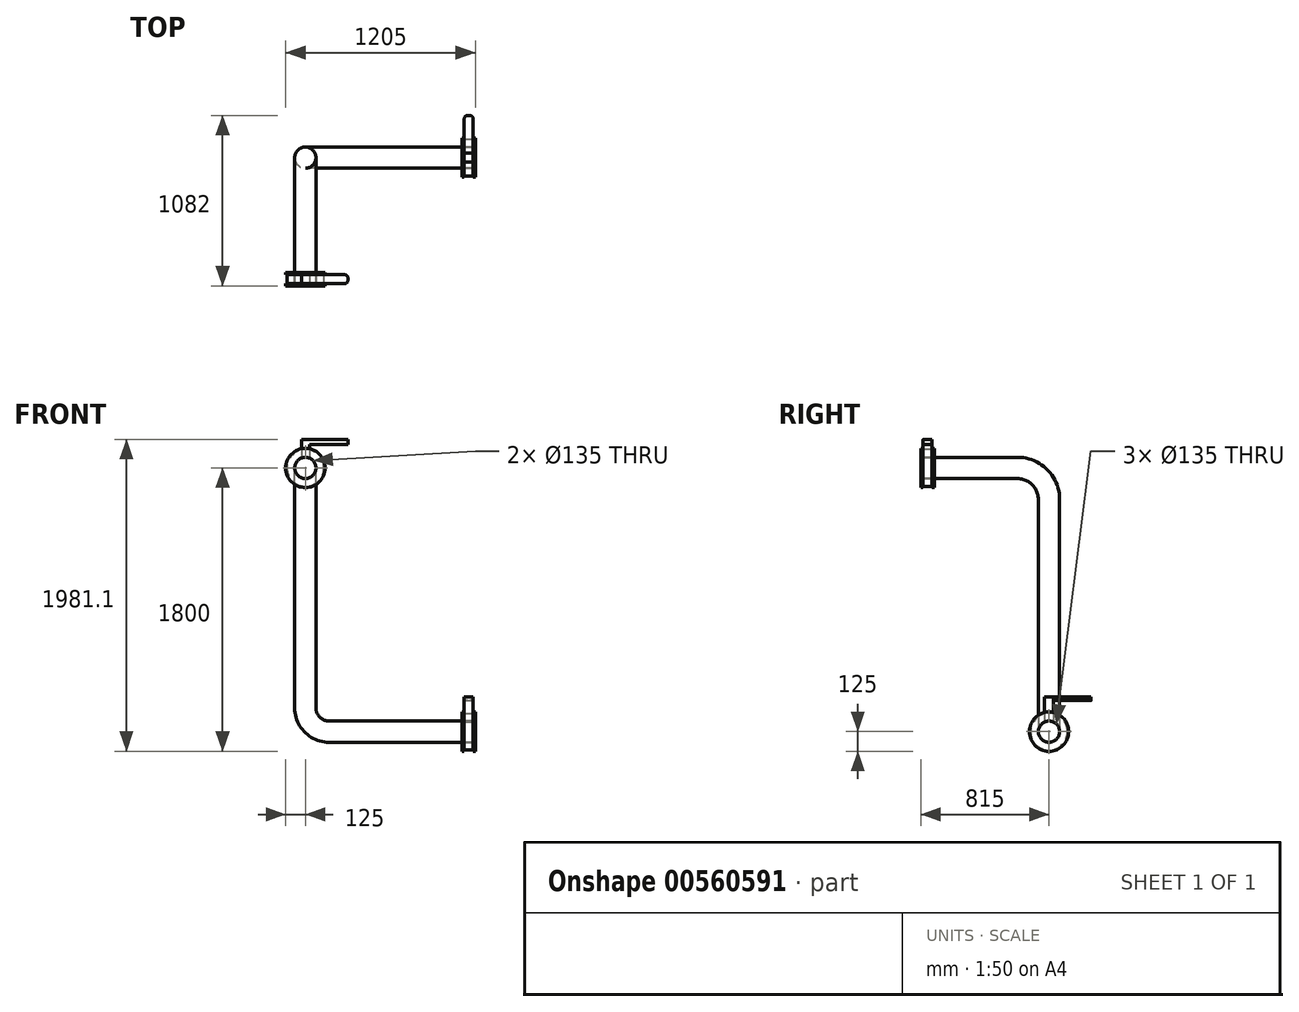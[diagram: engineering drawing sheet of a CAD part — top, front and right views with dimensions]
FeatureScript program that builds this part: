
annotation { "Feature Type Name" : "Feature", "Feature Type Description" : "" }
export const myFeature = defineFeature(function(context is Context, id is Id, definition is map)
    precondition{}
    {
        {
            var Q0;
            Q0=qCreatedBy(makeId("Front.planeOp"),FACE);
            var sketch = newSketch(context, id + "F0", { "sketchPlane" : qUnion([Q0])});
            skCircle(sketch, "E0", {"center": v(0, 0) * mm, "radius": 125 * mm});
            skCircle(sketch, "E1", {"center": v(0, 0) * mm, "radius": 67.5 * mm});
            skSolve(sketch);
        }
        {
            var Q0;
            Q0=qCreatedBy(makeId("Right.planeOp"),FACE);
            var sketch = newSketch(context, id + "F1", { "sketchPlane" : qUnion([Q0])});
            skLineSegment(sketch, "E2", {"start": v(0, 0) * mm, "end": v(600, 0) * mm});
            skLineSegment(sketch, "E3", {"start": v(800, -200) * mm, "end": v(800, -1675) * mm});
            skPoint(sketch, "E4.visualSharp", {"position": v(800, 0) * mm});
            skArc(sketch, "E4.filletArc", {"start": v(800, -200) * mm, "mid": v(741.42, -58.58) * mm, "end": v(600, 0) * mm});
            skSolve(sketch);
        }
        {
            var Q0;
            Q0=qCreatedBy(makeId("Front.planeOp"),FACE);
            cPlane(context, id + "F2", {"entities" : qUnion([Q0]), "cplaneType" : CPlaneType.OFFSET, "offset" : 800 * mm, "oppositeDirection" : true, "width" : 150 * mm, "height" : 150 * mm});
        }
        {
            var Q0;
            Q0=qCreatedBy(id+"F2.planeOp",FACE);
            var sketch = newSketch(context, id + "F3", { "sketchPlane" : qUnion([Q0])});
            skLineSegment(sketch, "E5.0", {"start": v(0, -200) * mm, "end": v(0, -1525) * mm});
            skLineSegment(sketch, "E6", {"start": v(150, -1675) * mm, "end": v(1080, -1675) * mm});
            skPoint(sketch, "E7.visualSharp", {"position": v(0, -1675) * mm});
            skArc(sketch, "E7.filletArc", {"start": v(0, -1525) * mm, "mid": v(43.93, -1631.07) * mm, "end": v(150, -1675) * mm});
            skSolve(sketch);
        }
        {
            var Q0;
            Q0=qCreatedBy(makeId("Right.planeOp"),FACE);
            cPlane(context, id + "F4", {"entities" : qUnion([Q0]), "cplaneType" : CPlaneType.OFFSET, "offset" : 1080 * mm, "width" : 150 * mm, "height" : 150 * mm});
        }
        {
            var Q0;
            Q0=qCreatedBy(id+"F4.planeOp",FACE);
            var sketch = newSketch(context, id + "F5", { "sketchPlane" : qUnion([Q0])});
            skPoint(sketch, "E8.0", {"position": v(800, -1675) * mm});
            skCircle(sketch, "E9", {"center": v(800, -1675) * mm, "radius": 67.5 * mm});
            skCircle(sketch, "E10", {"center": v(800, -1675) * mm, "radius": 125 * mm});
            skSolve(sketch);
        }
        {
            var Q0;
            Q0=makeQuery(id+"F0.imprint","IMPRINT",FACE,{"disambiguationData":[TD([[makeQuery(id+"F0.imprint","IMPRINT",EDGE,{"derivedFrom":sQuery(id+"F0.wireOp",EDGE,"E0")}),1.0]])]});
            var Q1;
            Q1=sQuery(id+"F0.wireOp",EDGE,"E0");
            extrude(context, id + "F6", {"entities" : qUnion([Q0]), "surfaceEntities" : qUnion([Q1]), "depth" : 15 * mm, "offsetDistance" : 25 * mm});
        }
        {
            var Q0;
            Q0=makeQuery(id+"F5.imprint","IMPRINT",FACE,{"disambiguationData":[TD([[makeQuery(id+"F5.imprint","IMPRINT",EDGE,{"derivedFrom":sQuery(id+"F5.wireOp",EDGE,"E9")}),-1.0]])]});
            extrude(context, id + "F7", {"entities" : qUnion([Q0]), "oppositeDirection" : true, "depth" : 15 * mm, "offsetDistance" : 25 * mm});
        }
        {
            var Q0;
            Q0=makeQuery(id+"F0.imprint","IMPRINT",FACE,{"disambiguationData":[TD([[makeQuery(id+"F0.imprint","IMPRINT",EDGE,{"derivedFrom":sQuery(id+"F0.wireOp",EDGE,"E0")}),1.0]])]});
            var sketch = newSketch(context, id + "F8", { "sketchPlane" : qUnion([Q0])});
            skCircle(sketch, "E11", {"center": v(0, 0) * mm, "radius": 117 * mm});
            skSolve(sketch);
        }
        {
            var Q0;
            Q0=makeQuery(id+"F8.imprint","IMPRINT",FACE,{"disambiguationData":[TD([[makeQuery(id+"F8.imprint","IMPRINT",EDGE,{"derivedFrom":sQuery(id+"F8.wireOp",EDGE,"E11")}),1.0]])]});
            extrude(context, id + "F9", {"entities" : qUnion([Q0]), "operationType" : NewBodyOperationType.ADD, "oppositeDirection" : true, "depth" : 56 * mm, "offsetDistance" : 25 * mm});
        }
        {
            var Q0;
            Q0=makeQuery(id+"F9.opExtrude","CAP_FACE",FACE,{"disambiguationData":[OSD([sQuery(id+"F0.wireOp",EDGE,"E1"),sQuery(id+"F8.wireOp",EDGE,"E11")])],"isStart":false});
            var sketch = newSketch(context, id + "F10", { "sketchPlane" : qUnion([Q0])});
            skCircle(sketch, "E12", {"center": v(0, 0) * mm, "radius": 125 * mm});
            skSolve(sketch);
        }
        {
            var Q0;
            Q0=makeQuery(id+"F10.imprint","IMPRINT",FACE,{"disambiguationData":[TD([[makeQuery(id+"F10.imprint","IMPRINT",EDGE,{"derivedFrom":sQuery(id+"F10.wireOp",EDGE,"E12")}),1.0]])]});
            var Q1;
            Q1=makeQuery(id+"F10.imprint","IMPRINT",FACE,{"disambiguationData":[TD([[makeQuery(id+"F10.imprint","IMPRINT",EDGE,{"derivedFrom":makeQuery(id+"F9.opExtrude","CAP_EDGE",EDGE,{"disambiguationData":[OSD([sQuery(id+"F8.wireOp",EDGE,"E11")])],"isStart":false})}),-1.0]])]});
            extrude(context, id + "F11", {"entities" : qUnion([Q0, Q1]), "depth" : 15 * mm, "offsetDistance" : 25 * mm});
        }
        {
            var Q0;
            Q0=makeQuery(id+"F0.imprint","IMPRINT",FACE,{"disambiguationData":[TD([[makeQuery(id+"F0.imprint","IMPRINT",EDGE,{"derivedFrom":sQuery(id+"F0.wireOp",EDGE,"E0")}),1.0]])]});
            var sketch = newSketch(context, id + "F12", { "sketchPlane" : qUnion([Q0])});
            skLineSegment(sketch, "E13.bottom", {"start": v(26.33, 181.1) * mm, "end": v(-25.2, 181.1) * mm});
            skLineSegment(sketch, "E13.top", {"start": v(26.33, 0) * mm, "end": v(-25.2, 0) * mm});
            skLineSegment(sketch, "E13.left", {"start": v(26.33, 181.1) * mm, "end": v(26.33, 0) * mm});
            skLineSegment(sketch, "E13.right", {"start": v(-25.2, 181.1) * mm, "end": v(-25.2, 0) * mm});
            skSolve(sketch);
        }
        {
            var Q0;
            {var subQ0=sQuery(id+"F12.wireOp",EDGE,"E13.bottom");Q0=makeQuery(id+"F12.imprint","IMPRINT",FACE,{"disambiguationData":[TD([[makeQuery(id+"F12.imprint","IMPRINT",EDGE,{"derivedFrom":subQ0}),1.0]])]});}
            var Q1;
            {var subQ0=sQuery(id+"F12.wireOp",EDGE,"E13.left");var subQ1=makeQuery(id+"F0.imprint","IMPRINT",EDGE,{"derivedFrom":sQuery(id+"F0.wireOp",EDGE,"E0")});var subQ2=makeQuery(id+"F12.imprint","INTERSECT",VERTEX,{"derivedFrom":[subQ1,subQ0]});Q1=makeQuery(id+"F12.imprint","IMPRINT",FACE,{"disambiguationData":[TD([[makeQuery(id+"F12.imprint","IMPRINT",EDGE,{"disambiguationData":[TD([[subQ2,-1.0]])],"derivedFrom":subQ0}),-1.0]])]});}
            extrude(context, id + "F13", {"entities" : qUnion([Q0, Q1]), "oppositeDirection" : true, "depth" : 56 * mm, "offsetDistance" : 25 * mm});
        }
        {
            var Q0;
            Q0=makeQuery(id+"F13.opExtrude","SWEPT_FACE",FACE,{"disambiguationData":[OSD([sQuery(id+"F12.wireOp",EDGE,"E13.bottom")])]});
            var sketch = newSketch(context, id + "F14", { "sketchPlane" : qUnion([Q0])});
            skLineSegment(sketch, "E14.bottom", {"start": v(-25.2, 56) * mm, "end": v(249.8, 56) * mm});
            skLineSegment(sketch, "E14.top", {"start": v(-25.2, 0) * mm, "end": v(249.8, 0) * mm});
            skLineSegment(sketch, "E14.left", {"start": v(-25.2, 56) * mm, "end": v(-25.2, 0) * mm});
            skLineSegment(sketch, "E14.right", {"start": v(269.8, 36) * mm, "end": v(269.8, 20) * mm});
            skPoint(sketch, "E15.visualSharp", {"position": v(269.8, 56) * mm});
            skArc(sketch, "E15.filletArc", {"start": v(269.8, 36) * mm, "mid": v(263.94, 50.14) * mm, "end": v(249.8, 56) * mm});
            skPoint(sketch, "E16.visualSharp", {"position": v(269.8, 0) * mm});
            skArc(sketch, "E16.filletArc", {"start": v(249.8, 0) * mm, "mid": v(263.94, 5.86) * mm, "end": v(269.8, 20) * mm});
            skSolve(sketch);
        }
        {
            var Q0;
            Q0=makeQuery(id+"F14.imprint","IMPRINT",FACE,{"disambiguationData":[TD([[makeQuery(id+"F14.imprint","IMPRINT",EDGE,{"derivedFrom":sQuery(id+"F14.wireOp",EDGE,"E14.right")}),-1.0]])]});
            extrude(context, id + "F15", {"entities" : qUnion([Q0]), "operationType" : NewBodyOperationType.ADD, "oppositeDirection" : true, "depth" : 32 * mm, "offsetDistance" : 25 * mm});
        }
        {
            var Q0;
            Q0=makeQuery(id+"F7.opExtrude","CAP_FACE",FACE,{"disambiguationData":[OSD([sQuery(id+"F5.wireOp",EDGE,"E9"),sQuery(id+"F5.wireOp",EDGE,"E10")])],"isStart":false});
            var sketch = newSketch(context, id + "F16", { "sketchPlane" : qUnion([Q0])});
            skCircle(sketch, "E17", {"center": v(-800, -1675) * mm, "radius": 117 * mm});
            skSolve(sketch);
        }
        {
            var Q0;
            Q0=makeQuery(id+"F16.imprint","IMPRINT",FACE,{"disambiguationData":[TD([[makeQuery(id+"F16.imprint","IMPRINT",EDGE,{"derivedFrom":sQuery(id+"F16.wireOp",EDGE,"E17")}),1.0]])]});
            extrude(context, id + "F17", {"entities" : qUnion([Q0]), "depth" : 56 * mm, "offsetDistance" : 25 * mm});
        }
        {
            var Q0;
            Q0=makeQuery(id+"F17.opExtrude","CAP_FACE",FACE,{"disambiguationData":[OSD([sQuery(id+"F5.wireOp",EDGE,"E9"),sQuery(id+"F16.wireOp",EDGE,"E17")])],"isStart":false});
            var sketch = newSketch(context, id + "F18", { "sketchPlane" : qUnion([Q0])});
            skCircle(sketch, "E18", {"center": v(-800, -1675) * mm, "radius": 125 * mm});
            skSolve(sketch);
        }
        {
            var Q0;
            Q0=makeQuery(id+"F18.imprint","IMPRINT",FACE,{"disambiguationData":[TD([[makeQuery(id+"F18.imprint","IMPRINT",EDGE,{"derivedFrom":sQuery(id+"F18.wireOp",EDGE,"E18")}),1.0]])]});
            var Q1;
            Q1=makeQuery(id+"F18.imprint","IMPRINT",FACE,{"disambiguationData":[TD([[makeQuery(id+"F18.imprint","IMPRINT",EDGE,{"derivedFrom":makeQuery(id+"F17.opExtrude","CAP_EDGE",EDGE,{"disambiguationData":[OSD([sQuery(id+"F16.wireOp",EDGE,"E17")])],"isStart":false})}),1.0]])]});
            extrude(context, id + "F19", {"entities" : qUnion([Q0, Q1]), "depth" : 15 * mm, "offsetDistance" : 25 * mm});
        }
        {
            var Q0;
            Q0=makeQuery(id+"F7.opExtrude","CAP_FACE",FACE,{"disambiguationData":[OSD([sQuery(id+"F5.wireOp",EDGE,"E9"),sQuery(id+"F5.wireOp",EDGE,"E10")])],"isStart":false});
            var sketch = newSketch(context, id + "F20", { "sketchPlane" : qUnion([Q0])});
            skLineSegment(sketch, "E19.bottom", {"start": v(-828, -1453) * mm, "end": v(-772, -1453) * mm});
            skLineSegment(sketch, "E19.top", {"start": v(-828, -1675) * mm, "end": v(-772, -1675) * mm});
            skLineSegment(sketch, "E19.left", {"start": v(-828, -1453) * mm, "end": v(-828, -1675) * mm});
            skLineSegment(sketch, "E19.right", {"start": v(-772, -1453) * mm, "end": v(-772, -1675) * mm});
            skSolve(sketch);
        }
        {
            var Q0;
            {var subQ0=sQuery(id+"F20.wireOp",EDGE,"E19.bottom");Q0=makeQuery(id+"F20.imprint","IMPRINT",FACE,{"disambiguationData":[TD([[makeQuery(id+"F20.imprint","IMPRINT",EDGE,{"derivedFrom":subQ0}),-1.0]])]});}
            var Q1;
            {var subQ0=sQuery(id+"F20.wireOp",EDGE,"E19.left");var subQ1=makeQuery(id+"F7.opExtrude","CAP_EDGE",EDGE,{"disambiguationData":[OSD([sQuery(id+"F5.wireOp",EDGE,"E10")])],"isStart":false});var subQ2=makeQuery(id+"F20.imprint","INTERSECT",VERTEX,{"derivedFrom":[subQ1,subQ0]});Q1=makeQuery(id+"F20.imprint","IMPRINT",FACE,{"disambiguationData":[TD([[makeQuery(id+"F20.imprint","IMPRINT",EDGE,{"disambiguationData":[TD([[subQ2,-1.0]])],"derivedFrom":subQ0}),1.0]])]});}
            extrude(context, id + "F21", {"entities" : qUnion([Q0, Q1]), "depth" : 56 * mm, "offsetDistance" : 25 * mm});
        }
        {
            var Q0;
            Q0=makeQuery(id+"F21.opExtrude","SWEPT_FACE",FACE,{"disambiguationData":[OSD([sQuery(id+"F20.wireOp",EDGE,"E19.bottom")])]});
            var sketch = newSketch(context, id + "F22", { "sketchPlane" : qUnion([Q0])});
            skLineSegment(sketch, "E20.bottom", {"start": v(1009, 772) * mm, "end": v(1065, 772) * mm});
            skLineSegment(sketch, "E20.top", {"start": v(1029, 1067) * mm, "end": v(1045, 1067) * mm});
            skLineSegment(sketch, "E20.left", {"start": v(1009, 772) * mm, "end": v(1009, 1047) * mm});
            skLineSegment(sketch, "E20.right", {"start": v(1065, 772) * mm, "end": v(1065, 1047) * mm});
            skPoint(sketch, "E21.visualSharp", {"position": v(1009, 1067) * mm});
            skArc(sketch, "E21.filletArc", {"start": v(1029, 1067) * mm, "mid": v(1014.86, 1061.14) * mm, "end": v(1009, 1047) * mm});
            skPoint(sketch, "E22.visualSharp", {"position": v(1065, 1067) * mm});
            skArc(sketch, "E22.filletArc", {"start": v(1065, 1047) * mm, "mid": v(1059.14, 1061.14) * mm, "end": v(1045, 1067) * mm});
            skSolve(sketch);
        }
        {
            var Q0;
            Q0=makeQuery(id+"F22.imprint","IMPRINT",FACE,{"disambiguationData":[TD([[makeQuery(id+"F22.imprint","IMPRINT",EDGE,{"derivedFrom":sQuery(id+"F22.wireOp",EDGE,"E20.top")}),-1.0]])]});
            extrude(context, id + "F23", {"entities" : qUnion([Q0]), "oppositeDirection" : true, "depth" : 25 * mm, "offsetDistance" : 25 * mm});
        }
        {
            var Q0;
            Q0=makeQuery(id+"F5.imprint","IMPRINT",FACE,{"disambiguationData":[TD([[makeQuery(id+"F5.imprint","IMPRINT",EDGE,{"derivedFrom":sQuery(id+"F5.wireOp",EDGE,"E9")}),1.0]])]});
            var Q1;
            Q1=sQuery(id+"F3.wireOp",EDGE,"E6");
            var Q2;
            Q2=sQuery(id+"F3.wireOp",EDGE,"E7.filletArc");
            var Q3;
            Q3=sQuery(id+"F3.wireOp",EDGE,"E5.0");
            var Q4;
            Q4=sQuery(id+"F1.wireOp",EDGE,"E4.filletArc");
            var Q5;
            Q5=sQuery(id+"F1.wireOp",EDGE,"E2");
            sweep(context, id + "F24", {"profiles" : qUnion([Q0]), "path" : qUnion([Q1, Q2, Q3, Q4, Q5])});
        }
    });
